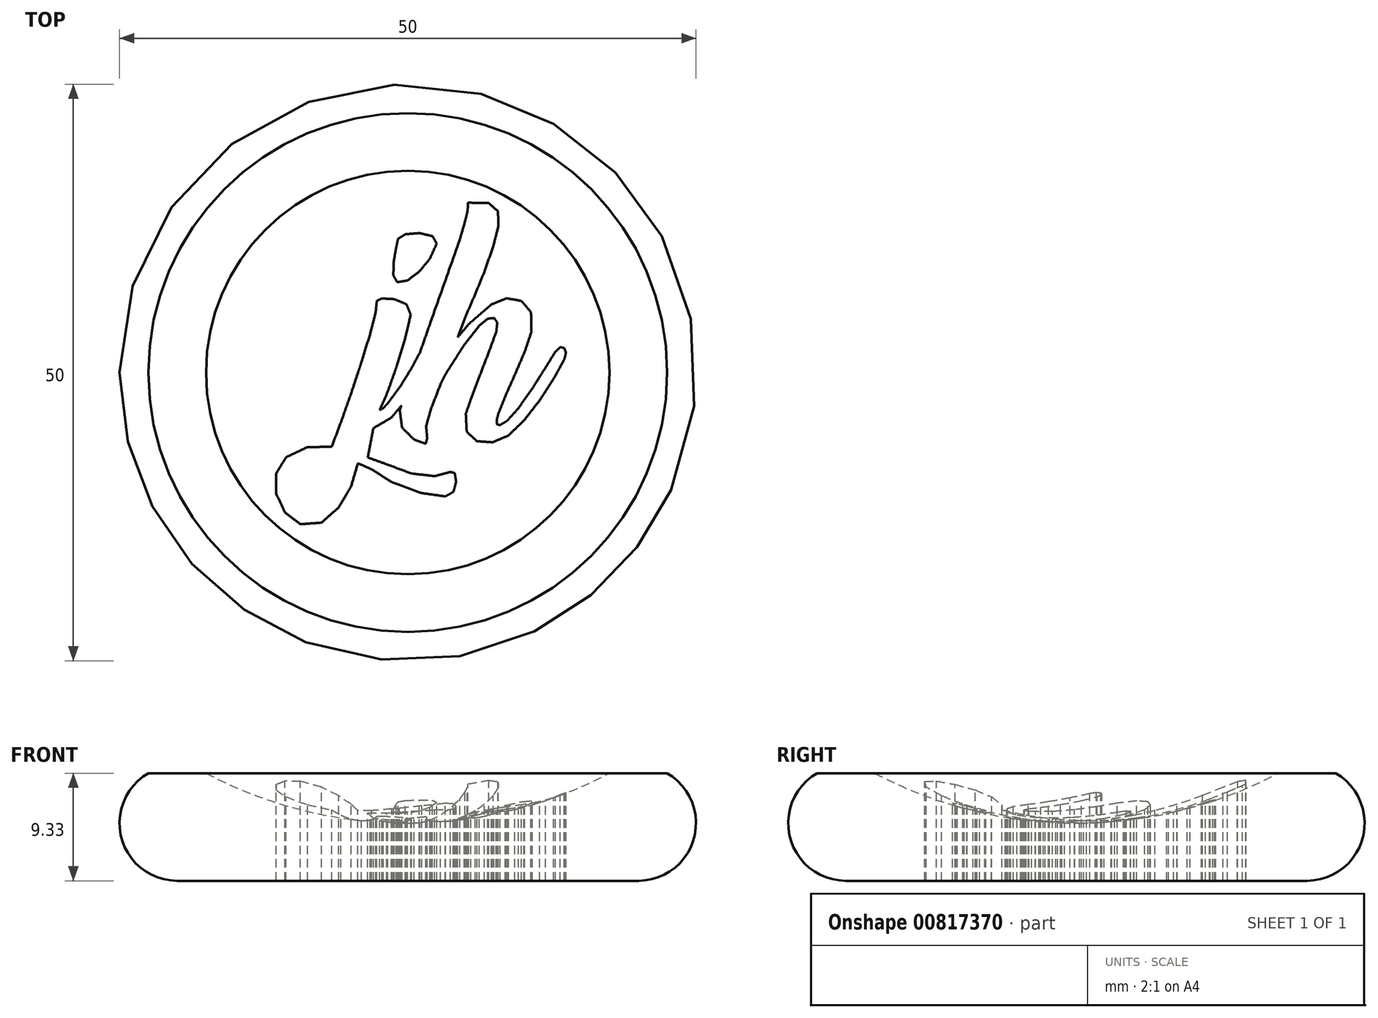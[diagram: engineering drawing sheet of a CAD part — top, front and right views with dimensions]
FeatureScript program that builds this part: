
annotation { "Feature Type Name" : "Feature", "Feature Type Description" : "" }
export const myFeature = defineFeature(function(context is Context, id is Id, definition is map)
    precondition{}
    {
        {
            var Q0;
            Q0=qCreatedBy(makeId("Front.planeOp"),FACE);
            var sketch = newSketch(context, id + "F0", { "sketchPlane" : qUnion([Q0])});
            skArc(sketch, "E0", {"start": v(-22.5, 9.33) * mm, "mid": v(-24.83, 3.73) * mm, "end": v(-20.04, 0) * mm});
            skArc(sketch, "E1", {"start": v(-17.5, 9.33) * mm, "mid": v(-9.01, 6.1) * mm, "end": v(0, 5) * mm});
            skLineSegment(sketch, "E2", {"start": v(-20.04, 0) * mm, "end": v(0, 0) * mm});
            skLineSegment(sketch, "E3", {"start": v(0, 0) * mm, "end": v(0, 5) * mm});
            skLineSegment(sketch, "E4.top", {"start": v(-22.5, 9.33) * mm, "end": v(-17.5, 9.33) * mm});
            skSolve(sketch);
        }
        {
            var Q0;
            Q0=makeQuery(id+"F0.imprint","IMPRINT",FACE,{"disambiguationData":[TD([[makeQuery(id+"F0.imprint","IMPRINT",EDGE,{"derivedFrom":sQuery(id+"F0.wireOp",EDGE,"E0")}),1.0]])]});
            var Q1;
            Q1=sQuery(id+"F0.wireOp",EDGE,"E3");
            revolve(context, id + "F1", {"surfaceOperationType" : NewSurfaceOperationType.NEW, "entities" : qUnion([Q0]), "axis" : qUnion([Q1]), "revolveType" : RevolveType.FULL});
        }
        {
            var Q0;
            Q0=makeQuery(id+"F1.opRevolve","SWEPT_FACE",FACE,{"disambiguationData":[OSD([sQuery(id+"F0.wireOp",EDGE,"E4.top")])]});
            var sketch = newSketch(context, id + "F2", { "sketchPlane" : qUnion([Q0])});
            skLineSegment(sketch, "E5", {"start": v(0.25, 5.01) * mm, "end": v(-0.22, 3) * mm});
            skLineSegment(sketch, "E6", {"start": v(-0.22, 3) * mm, "end": v(-0.93, 0.62) * mm});
            skLineSegment(sketch, "E7", {"start": v(-0.93, 0.62) * mm, "end": v(-1.72, -1.62) * mm});
            skLineSegment(sketch, "E8", {"start": v(-1.72, -1.62) * mm, "end": v(-2.42, -3.24) * mm});
            skLineSegment(sketch, "E9", {"start": v(-2.42, -3.24) * mm, "end": v(-2.12, -3.09) * mm});
            skLineSegment(sketch, "E10", {"start": v(-2.12, -3.09) * mm, "end": v(-1.78, -2.71) * mm});
            skLineSegment(sketch, "E11", {"start": v(-1.78, -2.71) * mm, "end": v(-0.69, -1.26) * mm});
            skLineSegment(sketch, "E12", {"start": v(-0.69, -1.26) * mm, "end": v(0.25, 0.26) * mm});
            skLineSegment(sketch, "E13", {"start": v(0.25, 0.26) * mm, "end": v(1, 1.64) * mm});
            skLineSegment(sketch, "E14", {"start": v(1, 1.64) * mm, "end": v(1.54, 2.68) * mm});
            skLineSegment(sketch, "E15", {"start": v(1.54, 2.68) * mm, "end": v(2, 3.32) * mm});
            skLineSegment(sketch, "E16", {"start": v(2, 3.32) * mm, "end": v(2.4, 3.32) * mm});
            skLineSegment(sketch, "E17", {"start": v(2.4, 3.32) * mm, "end": v(2.53, 2.77) * mm});
            skLineSegment(sketch, "E18", {"start": v(2.53, 2.77) * mm, "end": v(2.25, 1.8) * mm});
            skLineSegment(sketch, "E19", {"start": v(2.25, 1.8) * mm, "end": v(1.3, -0.02) * mm});
            skLineSegment(sketch, "E20", {"start": v(1.3, -0.02) * mm, "end": v(0.07, -2.11) * mm});
            skLineSegment(sketch, "E21", {"start": v(0.07, -2.11) * mm, "end": v(-1.4, -3.9) * mm});
            skLineSegment(sketch, "E22", {"start": v(-1.4, -3.9) * mm, "end": v(-2.99, -4.82) * mm});
            skLineSegment(sketch, "E23", {"start": v(-2.99, -4.82) * mm, "end": v(-3.47, -7.37) * mm});
            skLineSegment(sketch, "E24", {"start": v(-3.47, -7.37) * mm, "end": v(-1.85, -7.95) * mm});
            skLineSegment(sketch, "E25", {"start": v(-1.85, -7.95) * mm, "end": v(0.34, -8.76) * mm});
            skLineSegment(sketch, "E26", {"start": v(0.34, -8.76) * mm, "end": v(2.33, -8.98) * mm});
            skLineSegment(sketch, "E27", {"start": v(2.33, -8.98) * mm, "end": v(3.7, -8.62) * mm});
            skLineSegment(sketch, "E28", {"start": v(3.7, -8.62) * mm, "end": v(4.08, -8.71) * mm});
            skLineSegment(sketch, "E29", {"start": v(4.08, -8.71) * mm, "end": v(4.2, -9.48) * mm});
            skLineSegment(sketch, "E30", {"start": v(4.2, -9.48) * mm, "end": v(3.96, -10.34) * mm});
            skLineSegment(sketch, "E31", {"start": v(3.96, -10.34) * mm, "end": v(3.25, -10.74) * mm});
            skLineSegment(sketch, "E32", {"start": v(3.25, -10.74) * mm, "end": v(1.2, -10.45) * mm});
            skLineSegment(sketch, "E33", {"start": v(1.2, -10.45) * mm, "end": v(-0.73, -9.74) * mm});
            skLineSegment(sketch, "E34", {"start": v(-1.38, -9.51) * mm, "end": v(-3.13, -8.4) * mm});
            skLineSegment(sketch, "E35", {"start": v(-3.13, -8.4) * mm, "end": v(-4.33, -7.86) * mm});
            skLineSegment(sketch, "E36", {"start": v(-4.33, -7.86) * mm, "end": v(-4.9, -9.85) * mm});
            skLineSegment(sketch, "E37", {"start": v(-4.9, -9.85) * mm, "end": v(-6, -11.7) * mm});
            skLineSegment(sketch, "E38", {"start": v(-6, -11.7) * mm, "end": v(-7.47, -13.02) * mm});
            skLineSegment(sketch, "E39", {"start": v(-7.47, -13.02) * mm, "end": v(-9.32, -13.15) * mm});
            skLineSegment(sketch, "E40", {"start": v(-9.32, -13.15) * mm, "end": v(-10.65, -12.13) * mm});
            skLineSegment(sketch, "E41", {"start": v(-10.65, -12.13) * mm, "end": v(-11.4, -10.51) * mm});
            skLineSegment(sketch, "E42", {"start": v(-11.4, -10.51) * mm, "end": v(-11.43, -8.78) * mm});
            skLineSegment(sketch, "E43", {"start": v(-11.43, -8.78) * mm, "end": v(-10.56, -7.35) * mm});
            skLineSegment(sketch, "E44", {"start": v(-10.56, -7.35) * mm, "end": v(-8.7, -6.46) * mm});
            skLineSegment(sketch, "E45", {"start": v(-8.7, -6.46) * mm, "end": v(-6.6, -6.44) * mm});
            skLineSegment(sketch, "E46", {"start": v(-6.6, -6.44) * mm, "end": v(-5.81, -4.35) * mm});
            skLineSegment(sketch, "E47", {"start": v(-5.81, -4.35) * mm, "end": v(-4.9, -1.79) * mm});
            skLineSegment(sketch, "E48", {"start": v(-4.9, -1.79) * mm, "end": v(-4.02, 0.89) * mm});
            skLineSegment(sketch, "E49", {"start": v(-4.02, 0.89) * mm, "end": v(-3.27, 3.33) * mm});
            skLineSegment(sketch, "E50", {"start": v(-3.27, 3.33) * mm, "end": v(-2.78, 5.22) * mm});
            skLineSegment(sketch, "E51", {"start": v(-2.78, 5.22) * mm, "end": v(-2.68, 6.22) * mm});
            skLineSegment(sketch, "E52", {"start": v(-2.68, 6.22) * mm, "end": v(-2.25, 6.42) * mm});
            skLineSegment(sketch, "E53", {"start": v(-2.25, 6.42) * mm, "end": v(-1.16, 6.37) * mm});
            skLineSegment(sketch, "E54", {"start": v(-1.16, 6.37) * mm, "end": v(-0.1, 5.92) * mm});
            skLineSegment(sketch, "E55", {"start": v(-0.1, 5.92) * mm, "end": v(0.25, 5.01) * mm});
            skLineSegment(sketch, "E56", {"start": v(-9.7, -8.03) * mm, "end": v(-10.33, -9.18) * mm});
            skLineSegment(sketch, "E57", {"start": v(-10.33, -9.18) * mm, "end": v(-10.33, -10.23) * mm});
            skLineSegment(sketch, "E58", {"start": v(-10.33, -10.23) * mm, "end": v(-9.98, -11) * mm});
            skLineSegment(sketch, "E59", {"start": v(-9.98, -11) * mm, "end": v(-9.5, -11.34) * mm});
            skLineSegment(sketch, "E60", {"start": v(-9.5, -11.34) * mm, "end": v(-9.1, -11.36) * mm});
            skLineSegment(sketch, "E61", {"start": v(-9.1, -11.36) * mm, "end": v(-8.62, -11) * mm});
            skLineSegment(sketch, "E62", {"start": v(-8.62, -11) * mm, "end": v(-7.94, -9.85) * mm});
            skLineSegment(sketch, "E63", {"start": v(-7.94, -9.85) * mm, "end": v(-6.98, -7.46) * mm});
            skLineSegment(sketch, "E64", {"start": v(-6.98, -7.46) * mm, "end": v(-8.7, -7.5) * mm});
            skLineSegment(sketch, "E65", {"start": v(-8.7, -7.5) * mm, "end": v(-9.7, -8.03) * mm});
            skLineSegment(sketch, "E66", {"start": v(-0.84, 11.6) * mm, "end": v(-0.2, 12) * mm});
            skLineSegment(sketch, "E67", {"start": v(-0.2, 12) * mm, "end": v(1, 12.1) * mm});
            skLineSegment(sketch, "E68", {"start": v(1, 12.1) * mm, "end": v(2.14, 11.83) * mm});
            skLineSegment(sketch, "E69", {"start": v(2.14, 11.83) * mm, "end": v(2.52, 11.2) * mm});
            skLineSegment(sketch, "E70", {"start": v(2.52, 11.2) * mm, "end": v(1.91, 9.87) * mm});
            skLineSegment(sketch, "E71", {"start": v(1.91, 9.87) * mm, "end": v(0.99, 8.74) * mm});
            skLineSegment(sketch, "E72", {"start": v(0.99, 8.74) * mm, "end": v(-0.03, 7.99) * mm});
            skLineSegment(sketch, "E73", {"start": v(-0.03, 7.99) * mm, "end": v(-0.91, 7.84) * mm});
            skLineSegment(sketch, "E74", {"start": v(-0.91, 7.84) * mm, "end": v(-1.25, 8.44) * mm});
            skLineSegment(sketch, "E75", {"start": v(-1.25, 8.44) * mm, "end": v(-1.22, 9.6) * mm});
            skLineSegment(sketch, "E76", {"start": v(-1.22, 9.6) * mm, "end": v(-1, 10.83) * mm});
            skLineSegment(sketch, "E77", {"start": v(-1, 10.83) * mm, "end": v(-0.84, 11.6) * mm});
            skLineSegment(sketch, "E78", {"start": v(7.41, 10.93) * mm, "end": v(6.64, 8.72) * mm});
            skLineSegment(sketch, "E79", {"start": v(6.64, 8.72) * mm, "end": v(5.85, 6.8) * mm});
            skLineSegment(sketch, "E80", {"start": v(5.85, 6.8) * mm, "end": v(5.06, 4.97) * mm});
            skLineSegment(sketch, "E81", {"start": v(5.06, 4.97) * mm, "end": v(4.32, 3.05) * mm});
            skLineSegment(sketch, "E82", {"start": v(4.32, 3.05) * mm, "end": v(5.28, 4.2) * mm});
            skLineSegment(sketch, "E83", {"start": v(5.28, 4.2) * mm, "end": v(7.26, 5.92) * mm});
            skLineSegment(sketch, "E84", {"start": v(7.26, 5.92) * mm, "end": v(8.58, 6.44) * mm});
            skLineSegment(sketch, "E85", {"start": v(8.58, 6.44) * mm, "end": v(9.86, 6.22) * mm});
            skLineSegment(sketch, "E86", {"start": v(9.86, 6.22) * mm, "end": v(10.7, 5.24) * mm});
            skLineSegment(sketch, "E87", {"start": v(10.7, 5.24) * mm, "end": v(10.73, 3.54) * mm});
            skLineSegment(sketch, "E88", {"start": v(10.73, 3.54) * mm, "end": v(10.14, 1.8) * mm});
            skLineSegment(sketch, "E89", {"start": v(10.14, 1.8) * mm, "end": v(9.3, -0.17) * mm});
            skLineSegment(sketch, "E90", {"start": v(9.3, -0.17) * mm, "end": v(8.45, -2.07) * mm});
            skLineSegment(sketch, "E91", {"start": v(8.45, -2.07) * mm, "end": v(7.87, -3.54) * mm});
            skLineSegment(sketch, "E92", {"start": v(7.87, -3.54) * mm, "end": v(7.71, -4.1) * mm});
            skLineSegment(sketch, "E93", {"start": v(7.71, -4.1) * mm, "end": v(7.73, -4.48) * mm});
            skLineSegment(sketch, "E94", {"start": v(7.73, -4.48) * mm, "end": v(8, -4.56) * mm});
            skLineSegment(sketch, "E95", {"start": v(8, -4.56) * mm, "end": v(8.62, -4.18) * mm});
            skLineSegment(sketch, "E96", {"start": v(8.62, -4.18) * mm, "end": v(9.6, -3.09) * mm});
            skLineSegment(sketch, "E97", {"start": v(9.6, -3.09) * mm, "end": v(10.8, -1.38) * mm});
            skLineSegment(sketch, "E98", {"start": v(10.8, -1.38) * mm, "end": v(11.95, 0.43) * mm});
            skLineSegment(sketch, "E99", {"start": v(11.95, 0.43) * mm, "end": v(12.8, 1.8) * mm});
            skLineSegment(sketch, "E100", {"start": v(12.8, 1.8) * mm, "end": v(13.23, 2.2) * mm});
            skLineSegment(sketch, "E101", {"start": v(13.23, 2.2) * mm, "end": v(13.57, 2.13) * mm});
            skLineSegment(sketch, "E102", {"start": v(13.57, 2.13) * mm, "end": v(13.72, 1.73) * mm});
            skLineSegment(sketch, "E103", {"start": v(13.72, 1.73) * mm, "end": v(13.6, 1.17) * mm});
            skLineSegment(sketch, "E104", {"start": v(13.6, 1.17) * mm, "end": v(12.65, -0.55) * mm});
            skLineSegment(sketch, "E105", {"start": v(12.65, -0.55) * mm, "end": v(11.43, -2.43) * mm});
            skLineSegment(sketch, "E106", {"start": v(11.43, -2.43) * mm, "end": v(10.07, -4.16) * mm});
            skLineSegment(sketch, "E107", {"start": v(10.07, -4.16) * mm, "end": v(8.73, -5.46) * mm});
            skLineSegment(sketch, "E108", {"start": v(8.73, -5.46) * mm, "end": v(7.34, -6.05) * mm});
            skLineSegment(sketch, "E109", {"start": v(7.34, -6.05) * mm, "end": v(6, -5.95) * mm});
            skLineSegment(sketch, "E110", {"start": v(6, -5.95) * mm, "end": v(5.11, -5.14) * mm});
            skLineSegment(sketch, "E111", {"start": v(5.11, -5.14) * mm, "end": v(5.04, -3.58) * mm});
            skLineSegment(sketch, "E112", {"start": v(5.04, -3.58) * mm, "end": v(5.47, -2.32) * mm});
            skLineSegment(sketch, "E113", {"start": v(5.47, -2.32) * mm, "end": v(6.2, -0.36) * mm});
            skLineSegment(sketch, "E114", {"start": v(6.2, -0.36) * mm, "end": v(7.04, 1.79) * mm});
            skLineSegment(sketch, "E115", {"start": v(7.04, 1.79) * mm, "end": v(7.68, 3.54) * mm});
            skLineSegment(sketch, "E116", {"start": v(7.68, 3.54) * mm, "end": v(7.77, 4.33) * mm});
            skLineSegment(sketch, "E117", {"start": v(7.77, 4.33) * mm, "end": v(7.49, 4.73) * mm});
            skLineSegment(sketch, "E118", {"start": v(7.49, 4.73) * mm, "end": v(6.92, 4.67) * mm});
            skLineSegment(sketch, "E119", {"start": v(6.92, 4.67) * mm, "end": v(6.2, 4.07) * mm});
            skLineSegment(sketch, "E120", {"start": v(6.2, 4.07) * mm, "end": v(4.9, 2.41) * mm});
            skLineSegment(sketch, "E121", {"start": v(4.9, 2.41) * mm, "end": v(3.27, -0.15) * mm});
            skLineSegment(sketch, "E122", {"start": v(3.27, -0.15) * mm, "end": v(2.84, -1.04) * mm});
            skLineSegment(sketch, "E123", {"start": v(2.84, -1.04) * mm, "end": v(2.02, -3.13) * mm});
            skLineSegment(sketch, "E124", {"start": v(2.02, -3.13) * mm, "end": v(1.6, -4.65) * mm});
            skLineSegment(sketch, "E125", {"start": v(1.6, -4.65) * mm, "end": v(1.69, -5.69) * mm});
            skLineSegment(sketch, "E126", {"start": v(1.69, -5.69) * mm, "end": v(1.55, -6.18) * mm});
            skLineSegment(sketch, "E127", {"start": v(1.55, -6.18) * mm, "end": v(0.54, -5.8) * mm});
            skLineSegment(sketch, "E128", {"start": v(0.54, -5.8) * mm, "end": v(-0.5, -4.77) * mm});
            skLineSegment(sketch, "E129", {"start": v(-0.5, -4.77) * mm, "end": v(-0.69, -3.24) * mm});
            skLineSegment(sketch, "E130", {"start": v(-0.69, -3.24) * mm, "end": v(1.87, 4.07) * mm});
            skLineSegment(sketch, "E131", {"start": v(1.87, 4.07) * mm, "end": v(4.51, 11.53) * mm});
            skLineSegment(sketch, "E132", {"start": v(4.51, 11.53) * mm, "end": v(4.96, 13.1) * mm});
            skLineSegment(sketch, "E133", {"start": v(4.96, 13.1) * mm, "end": v(5.17, 13.94) * mm});
            skLineSegment(sketch, "E134", {"start": v(5.17, 13.94) * mm, "end": v(5.23, 14.4) * mm});
            skLineSegment(sketch, "E135", {"start": v(5.23, 14.4) * mm, "end": v(5.23, 14.73) * mm});
            skLineSegment(sketch, "E136", {"start": v(5.23, 14.73) * mm, "end": v(7.02, 14.7) * mm});
            skLineSegment(sketch, "E137", {"start": v(7.02, 14.7) * mm, "end": v(7.83, 14) * mm});
            skLineSegment(sketch, "E138", {"start": v(7.83, 14) * mm, "end": v(7.87, 12.72) * mm});
            skLineSegment(sketch, "E139", {"start": v(7.87, 12.72) * mm, "end": v(7.41, 10.93) * mm});
            skLineSegment(sketch, "E140", {"start": v(-1.38, -9.51) * mm, "end": v(-0.73, -9.74) * mm});
            skSolve(sketch);
        }
        {
            var Q0;
            Q0=makeQuery(id+"F2.imprint","IMPRINT",FACE,{"disambiguationData":[TD([[makeQuery(id+"F2.imprint","IMPRINT",EDGE,{"derivedFrom":sQuery(id+"F2.wireOp",EDGE,"E5")}),-1.0]])]});
            var Q1;
            Q1=makeQuery(id+"F2.imprint","IMPRINT",FACE,{"disambiguationData":[TD([[makeQuery(id+"F2.imprint","IMPRINT",EDGE,{"derivedFrom":sQuery(id+"F2.wireOp",EDGE,"E56")}),1.0]])]});
            var Q2;
            Q2=makeQuery(id+"F2.imprint","IMPRINT",FACE,{"disambiguationData":[TD([[makeQuery(id+"F2.imprint","IMPRINT",EDGE,{"derivedFrom":sQuery(id+"F2.wireOp",EDGE,"E66")}),-1.0]])]});
            var Q3;
            {var subQ4=sQuery(id+"F2.wireOp",EDGE,"E15");Q3=makeQuery(id+"F2.imprint","IMPRINT",FACE,{"disambiguationData":[TD([[makeQuery(id+"F2.imprint","IMPRINT",EDGE,{"derivedFrom":subQ4}),1.0]])]});}
            var Q4;
            {var subQ0=sQuery(id+"F2.wireOp",EDGE,"E15");Q4=makeQuery(id+"F2.imprint","IMPRINT",FACE,{"disambiguationData":[TD([[makeQuery(id+"F2.imprint","IMPRINT",EDGE,{"derivedFrom":subQ0}),-1.0]])]});}
            extrude(context, id + "F3", {"entities" : qUnion([Q0, Q1, Q2, Q3, Q4]), "operationType" : NewBodyOperationType.REMOVE, "oppositeDirection" : true, "depth" : 25 * mm, "offsetDistance" : 25 * mm});
        }
    });
